# Revit family: K10.2 - Yoke Mount
name_source: partatom
category: Generic Models
revit_build: Autodesk Revit 2017 (Build: 20190508_0315(x64)
units: mm (PartAtom-declared; Revit-internal decimal feet)

## family parameters
Can host rebar = No
Cut with Voids When Loaded = No
Host = Face
Part Type = Normal
Room Calculation Point = No
Round Connector Dimension = Use Diameter
Shared = No

## types (4) — shared parameters
Coverage Horizontal = 90.00°
Coverage Vertical = 90.00°
Depth = 300 mm
Description = Multi-purpose, 2-way active loudspeaker
Height = 519 mm
Manufacturer = QSC, LLC
Manufacturer URL = www.qsc.com
Model = K10.2
Mount Depth = 401 mm
Mount Width = 115 mm
Product Documentation Link = https://www.qsc.com
Product Page URL = https://www.qsc.com
Regulatory Compliance = CE, RAEE, UL, China RoHS, RoHS II, FCC Class B
SPL Max = 130
Weight Dimensional (kg) = 17.6
Weight Dimensional (lb) = 38.8
Weight Product (kg) = 14.5
Weight Product (lb) = 32
Width = 320 mm  [stored 1.04987 ft]
zero-valued in all types: Default Elevation

## per-type parameters (varying)
| type | End Pivot Speaker Distance From Mount | Outer Yoke Width | Show End Pivot Model | Show Side Pivot Model | Side Pivot Speaker Distance From Mount |
| Side-Pivot, Furthest Position | 265 mm | 357 mm  [stored 1.17126 ft] | No | Yes | 305 mm |
| Side-Pivot, Nearest Position | 265 mm | 357 mm  [stored 1.17126 ft] | No | Yes | 232 mm  [stored 0.761155 ft] |
| End-Pivot, Furthest Position | 301 mm  [stored 0.987533 ft] | 568 mm  [stored 1.86352 ft] | Yes | No | 260 mm |
| End-Pivot, Nearest Position | 229 mm | 568 mm  [stored 1.86352 ft] | Yes | No | 260 mm |

note: [stored X ft] marks values corroborated as IEEE doubles in the binary element streams (Revit-internal decimal feet)

## geometry (parser evidence)
native form markers: Sweep x12
no freeform markers — native parametric forms only
